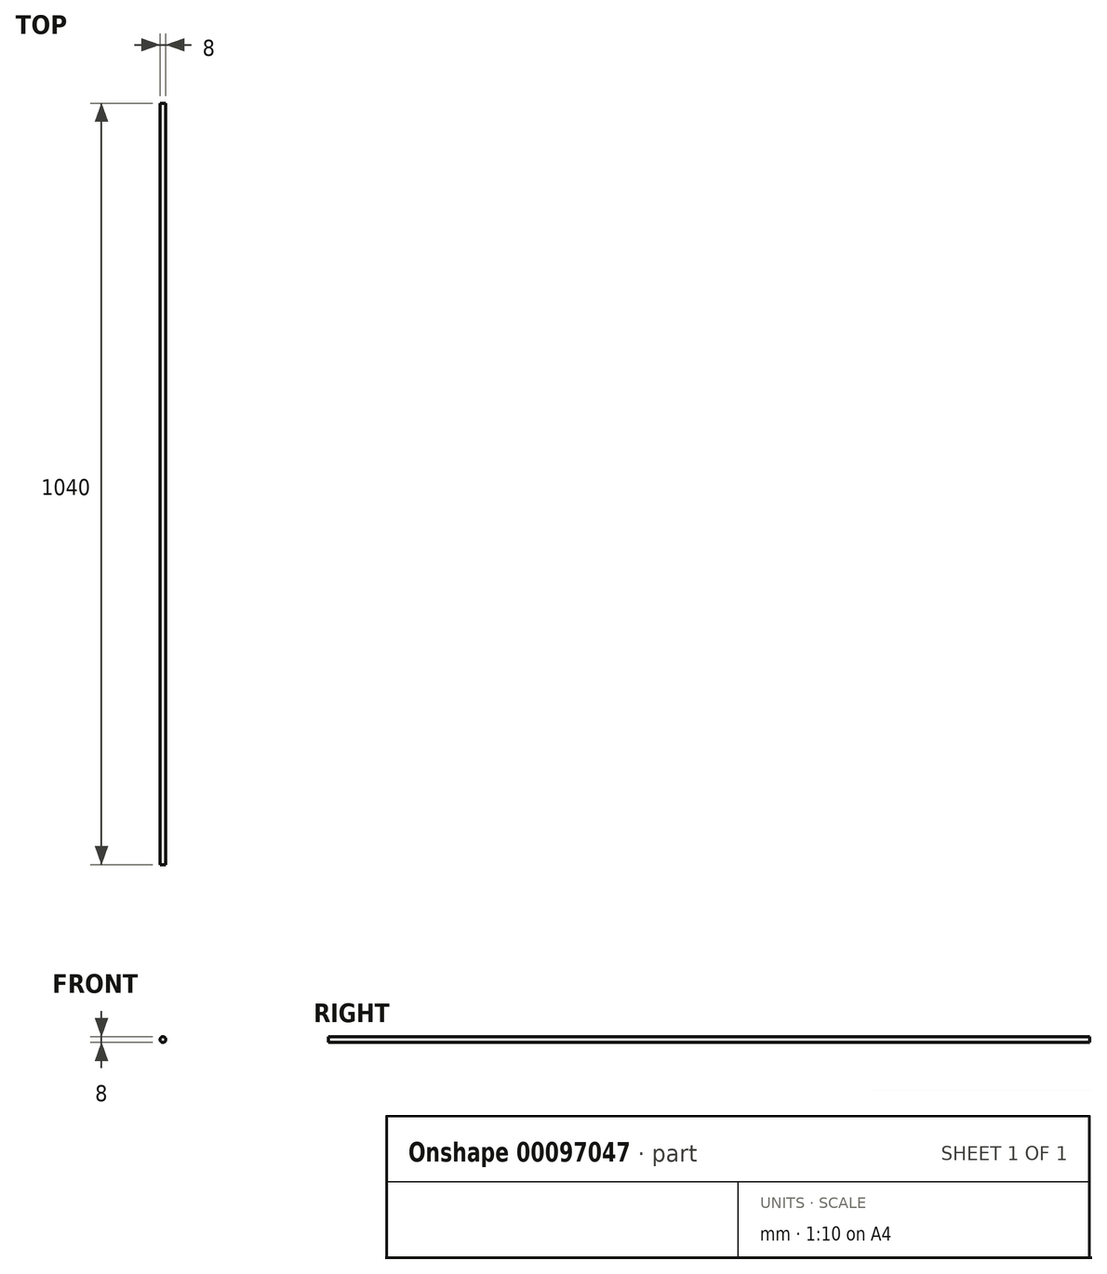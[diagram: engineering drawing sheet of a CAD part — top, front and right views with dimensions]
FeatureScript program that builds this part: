
annotation { "Feature Type Name" : "Feature", "Feature Type Description" : "" }
export const myFeature = defineFeature(function(context is Context, id is Id, definition is map)
    precondition{}
    {
        {
            var Q0;
            Q0=qCreatedBy(makeId("Front.planeOp"),FACE);
            var sketch = newSketch(context, id + "F0", { "sketchPlane" : qUnion([Q0])});
            skCircle(sketch, "E0", {"center": v(0, 0) * mm, "radius": 4 * mm});
            skSolve(sketch);
        }
        {
            var Q0;
            Q0=qSketchRegion(id+"F0",true);
            extrude(context, id + "F1", {"entities" : qUnion([Q0]), "depth" : 1040 * mm});
        }
    });
